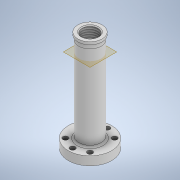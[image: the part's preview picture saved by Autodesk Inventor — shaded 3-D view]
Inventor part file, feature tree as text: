
AUTODESK INVENTOR PART (.ipt)
format: ipt  version: 2022.2 (Build 262287000, 287)  size: 178,688 bytes
history: native  units: mm
features: thread x7, extrude x4, sketch x4, projected_geometry x3, fillet x2, chamfer x2, other x1, plane x1
ambient origin geometry x8: Origin, YZ Plane, XZ Plane, XY Plane, X Axis, Y Axis, Z Axis, Center Point
bodies: Body1 (feature_tree)
feature tree (24):
  other  "Sólido1"
  extrude  "Extrusión1"  Depth=40.0mm
  extrude  "Extrusión2"  TaperAngle=45.0deg  [1 undecoded]
  fillet  "Empalme1"  Radius=6.0mm
  chamfer  "Chaflán1"  Distance=10.0mm
  extrude  "Extrusión4"  Depth=1.0mm
  fillet  "Empalme3"  Radius=26.0mm
  thread  "Thread1"  [1 undecoded]
  thread  "Thread2"  [1 undecoded]
  thread  "Thread3"  [1 undecoded]
  thread  "Thread4"  [1 undecoded]
  thread  "Thread5"  [1 undecoded]
  thread  "Thread6"  [1 undecoded]
  chamfer  "Chamfer2"  Distance=10.0mm
  plane  "Work Plane1"
  extrude  "Extrusion5"  Depth=10.0mm TaperAngle=0.0deg
  thread  "Thread7"  [1 undecoded]
  sketch  "Boceto1"  dims[d0=50.0mm d1=40.0mm]
  sketch  "Boceto2"  dims[d2=6.0mm d3=45.0deg d4=6.0mm]
  sketch  "Boceto4"  dims[d5=45.0deg]
  sketch  "Sketch5"  dims[d6=6.0mm d7=10.0mm d8=0.0mm d9=18.3mm d10=26.0mm d11=106.0mm d12=0.0mm d13=2.0mm d15=1.0mm d16=2.0mm d17=45.0deg d22=28.0mm d23=3.0mm d24=0.0mm d25=12.0mm d26=10.0mm d27=0.0mm d28=10.0mm d29=0.0mm d30=10.0mm d31=0.0mm d32=10.0mm d33=0.0mm d34=10.0mm d35=0.0mm d36=10.0mm d37=0.0mm d38=6.0mm d39=2.0mm d40=45.0deg d41=-20.0mm d43=1.7mm d44=1.0mm d45=0.0mm d46=18.0mm d47=0.0mm]
  projected_geometry  "Projected Loop1"
  projected_geometry  "Projected Loop2"
  projected_geometry  "Projected Loop3"
note: 8 required parameter values undecoded (feature->parameter linkage not recoverable at this tier; creation-order binding heuristic only, values carry confidence <= 0.55)
